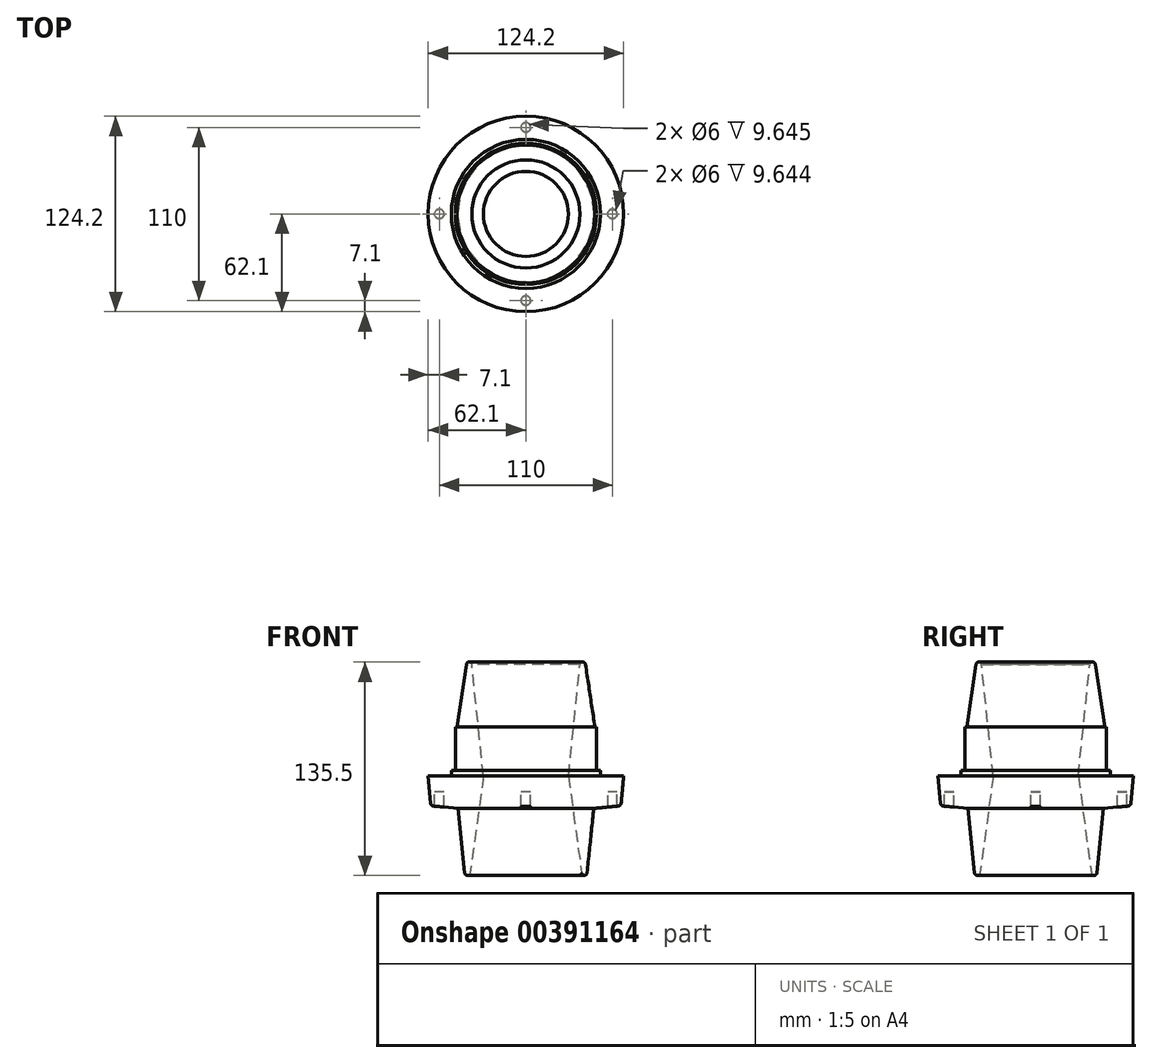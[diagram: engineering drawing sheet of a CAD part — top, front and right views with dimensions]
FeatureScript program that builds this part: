
annotation { "Feature Type Name" : "Feature", "Feature Type Description" : "" }
export const myFeature = defineFeature(function(context is Context, id is Id, definition is map)
    precondition{}
    {
        {
            var Q0;
            Q0=qCreatedBy(makeId("Front.planeOp"),FACE);
            var sketch = newSketch(context, id + "F0", { "sketchPlane" : qUnion([Q0])});
            skLineSegment(sketch, "E0", {"start": v(0, 66.16) * mm, "end": v(0, -69.97) * mm, "construction": true});
            skLineSegment(sketch, "E1", {"start": v(47.35, 0) * mm, "end": v(62.1, 0) * mm});
            skLineSegment(sketch, "E2", {"start": v(62.1, 0) * mm, "end": v(60.5, -17.2) * mm});
            skLineSegment(sketch, "E3", {"start": v(58.7, -19) * mm, "end": v(43.1, -20.5) * mm});
            skLineSegment(sketch, "E4", {"start": v(43.1, -20.5) * mm, "end": v(38.85, -61.43) * mm});
            skLineSegment(sketch, "E5", {"start": v(27, 0) * mm, "end": v(34.37, 71.01) * mm});
            skLineSegment(sketch, "E6", {"start": v(37.83, 71.01) * mm, "end": v(43.85, 31.2) * mm});
            skLineSegment(sketch, "E7", {"start": v(44.85, 31.2) * mm, "end": v(44.85, 3.5) * mm});
            skLineSegment(sketch, "E8", {"start": v(44.85, 3.5) * mm, "end": v(47.35, 3.5) * mm});
            skLineSegment(sketch, "E9", {"start": v(47.35, 3.5) * mm, "end": v(47.35, 0) * mm});
            skArc(sketch, "E10", {"start": v(58.7, -19) * mm, "mid": v(59.92, -18.42) * mm, "end": v(60.5, -17.2) * mm});
            skArc(sketch, "E11", {"start": v(37.83, 71.01) * mm, "mid": v(36.1, 72.5) * mm, "end": v(34.37, 71.01) * mm});
            skLineSegment(sketch, "E12", {"start": v(44.85, 31.2) * mm, "end": v(43.85, 31.2) * mm});
            skLineSegment(sketch, "E13", {"start": v(44.85, 3.5) * mm, "end": v(44.85, 31.2) * mm});
            skLineSegment(sketch, "E14", {"start": v(19.4, 72.5) * mm, "end": v(46.46, 72.5) * mm, "construction": true});
            skPoint(sketch, "E14.startSnap0", {"position": v(36.1, 72.5) * mm});
            skArc(sketch, "E15", {"start": v(35.38, -61.49) * mm, "mid": v(37.14, -63) * mm, "end": v(38.85, -61.43) * mm});
            skLineSegment(sketch, "E16", {"start": v(27, 0) * mm, "end": v(35.38, -61.49) * mm});
            skLineSegment(sketch, "E17", {"start": v(13.71, -63) * mm, "end": v(60.6, -63) * mm, "construction": true});
            skPoint(sketch, "E17.startSnap0", {"position": v(37.14, -63) * mm});
            skText(sketch, "E18", { "text": "7 navoja\ntrapezni navoj, precnik 95 mm, korak 4 mm\nu dnu trapezni\nali vrh zupca sa R=1 mm (potpuno zaobljen)", "fontName": "OpenSans-Regular.ttf"});
            skLineSegment(sketch, "E19", {"start": v(59.64, 30.67) * mm, "end": v(44.85, 17.35) * mm, "construction": true});
            const initialGuessF0  = {"E18": [0.06075, 0.0355, 1, 0, 0.00177]};
            skSetInitialGuess(sketch, initialGuessF0);
            skSolve(sketch);
        }
        {
            var Q0;
            Q0=makeQuery(id+"F0.imprint","IMPRINT",FACE,{"disambiguationData":[TD([[makeQuery(id+"F0.imprint","IMPRINT",EDGE,{"derivedFrom":sQuery(id+"F0.wireOp",EDGE,"E1")}),-1.0]])]});
            var Q1;
            Q1=sQuery(id+"F0.wireOp",EDGE,"E0");
            revolve(context, id + "F1", {"entities" : qUnion([Q0]), "axis" : qUnion([Q1]), "revolveType" : RevolveType.FULL});
        }
        {
            var Q0;
            Q0=qCreatedBy(makeId("Top.planeOp"),FACE);
            var sketch = newSketch(context, id + "F2", { "sketchPlane" : qUnion([Q0])});
            skCircle(sketch, "E20", {"center": v(0, 55) * mm, "radius": 3 * mm});
            skCircle(sketch, "E21", {"center": v(55, 0) * mm, "radius": 3 * mm});
            skCircle(sketch, "E22", {"center": v(0, -55) * mm, "radius": 3 * mm});
            skCircle(sketch, "E23", {"center": v(-55, 0) * mm, "radius": 3 * mm});
            skSolve(sketch);
        }
        {
            var Q0;
            Q0=makeQuery(id+"F2.imprint","IMPRINT",FACE,{"disambiguationData":[TD([[makeQuery(id+"F2.imprint","IMPRINT",EDGE,{"derivedFrom":sQuery(id+"F2.wireOp",EDGE,"E20")}),1.0]])]});
            var Q1;
            Q1=makeQuery(id+"F2.imprint","IMPRINT",FACE,{"disambiguationData":[TD([[makeQuery(id+"F2.imprint","IMPRINT",EDGE,{"derivedFrom":sQuery(id+"F2.wireOp",EDGE,"E23")}),1.0]])]});
            var Q2;
            Q2=makeQuery(id+"F2.imprint","IMPRINT",FACE,{"disambiguationData":[TD([[makeQuery(id+"F2.imprint","IMPRINT",EDGE,{"derivedFrom":sQuery(id+"F2.wireOp",EDGE,"E21")}),1.0]])]});
            var Q3;
            Q3=makeQuery(id+"F2.imprint","IMPRINT",FACE,{"disambiguationData":[TD([[makeQuery(id+"F2.imprint","IMPRINT",EDGE,{"derivedFrom":sQuery(id+"F2.wireOp",EDGE,"E22")}),1.0]])]});
            extrude(context, id + "F3", {"entities" : qUnion([Q0, Q1, Q2, Q3]), "operationType" : NewBodyOperationType.REMOVE, "oppositeDirection" : true, "depth" : 30 * mm, "hasSecondDirection" : true, "secondDirectionOppositeDirection" : true, "secondDirectionDepth" : 10 * mm});
        }
    });
